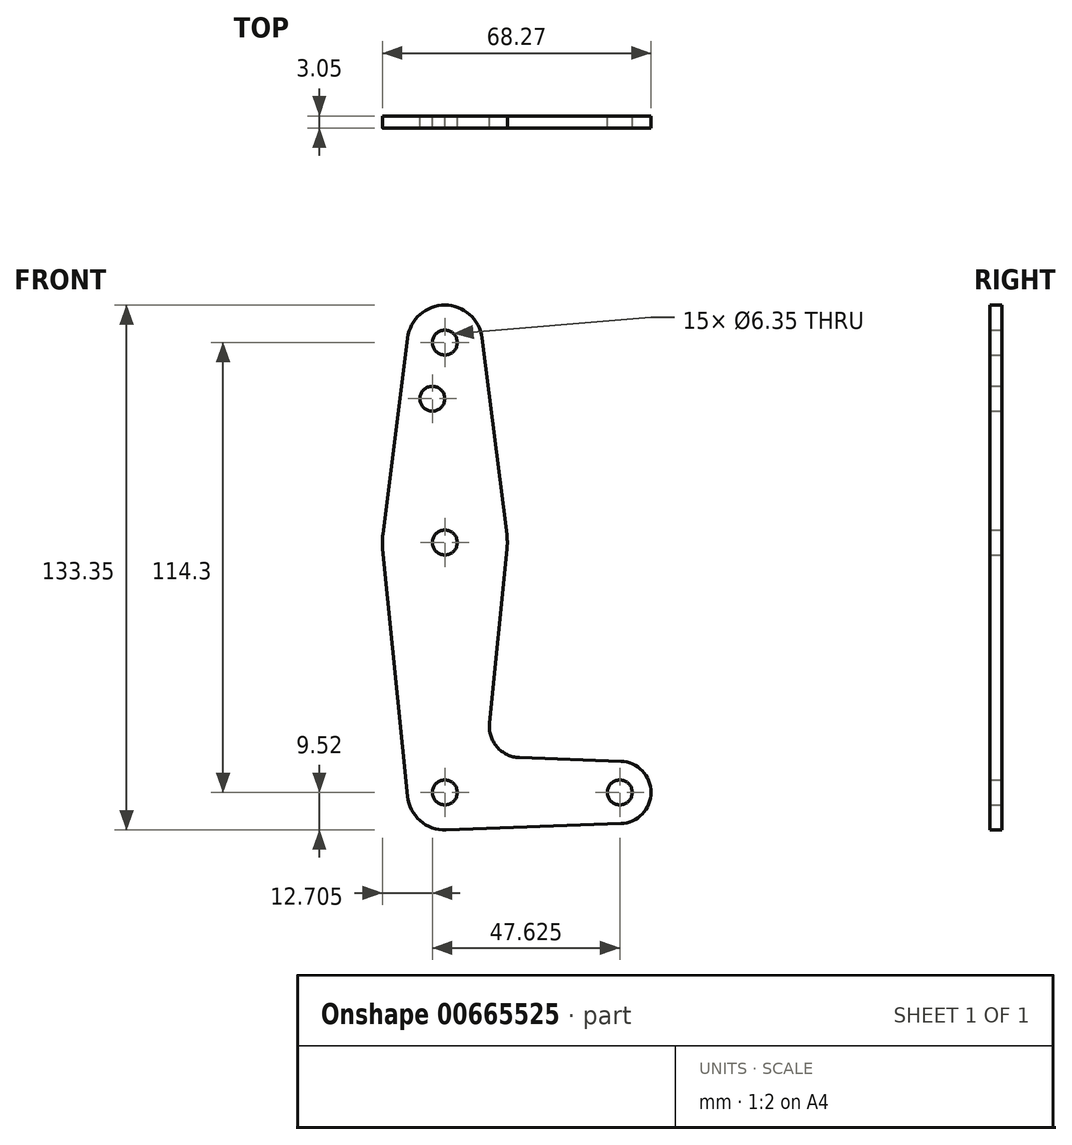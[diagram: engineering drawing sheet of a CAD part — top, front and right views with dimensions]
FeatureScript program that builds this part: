
annotation { "Feature Type Name" : "Feature", "Feature Type Description" : "" }
export const myFeature = defineFeature(function(context is Context, id is Id, definition is map)
    precondition{}
    {
        {
            var Q0;
            Q0=qCreatedBy(makeId("Front.planeOp"),FACE);
            var sketch = newSketch(context, id + "F0", { "sketchPlane" : qUnion([Q0])});
            skLineSegment(sketch, "E0", {"start": v(0, 114.3) * mm, "end": v(0, 0) * mm, "construction": true});
            skLineSegment(sketch, "E1", {"start": v(0, 0) * mm, "end": v(44.45, 0) * mm, "construction": true});
            skCircle(sketch, "E2", {"center": v(0, 114.3) * mm, "radius": 9.53 * mm});
            skCircle(sketch, "E3", {"center": v(0, 63.5) * mm, "radius": 15.88 * mm});
            skCircle(sketch, "E4", {"center": v(0, 0) * mm, "radius": 9.53 * mm});
            skCircle(sketch, "E5", {"center": v(44.45, 0) * mm, "radius": 7.94 * mm});
            skLineSegment(sketch, "E6", {"start": v(-9.45, 115.5) * mm, "end": v(-15.75, 65.48) * mm});
            skLineSegment(sketch, "E7", {"start": v(9.45, 115.5) * mm, "end": v(15.75, 65.48) * mm});
            skLineSegment(sketch, "E8", {"start": v(-15.8, 61.91) * mm, "end": v(-9.48, -0.95) * mm});
            skLineSegment(sketch, "E9", {"start": v(15.8, 61.91) * mm, "end": v(9.57, 0) * mm});
            skLineSegment(sketch, "E10", {"start": v(0.34, 9.52) * mm, "end": v(44.73, 7.93) * mm});
            skLineSegment(sketch, "E11", {"start": v(0.34, -9.52) * mm, "end": v(44.73, -7.93) * mm});
            skCircle(sketch, "E12", {"center": v(0, 114.3) * mm, "radius": 3.18 * mm});
            skCircle(sketch, "E13", {"center": v(-3.17, 100.03) * mm, "radius": 3.18 * mm});
            skCircle(sketch, "E14", {"center": v(0, 63.5) * mm, "radius": 3.18 * mm});
            skCircle(sketch, "E15", {"center": v(0, 0) * mm, "radius": 3.18 * mm});
            skCircle(sketch, "E16", {"center": v(44.45, 0) * mm, "radius": 3.18 * mm});
            skArc(sketch, "E17", {"start": v(11.34, 17.6) * mm, "mid": v(13.26, 11.57) * mm, "end": v(18.97, 8.85) * mm});
            skSolve(sketch);
        }
        {
            var Q0;
            Q0 = qSketchRegion(id + "F0", true);
            extrude(context, id + "F1", {"entities" : qUnion([Q0]), "depth" : 3.05 * mm, "offsetDistance" : 25.4 * mm});
        }
    });
